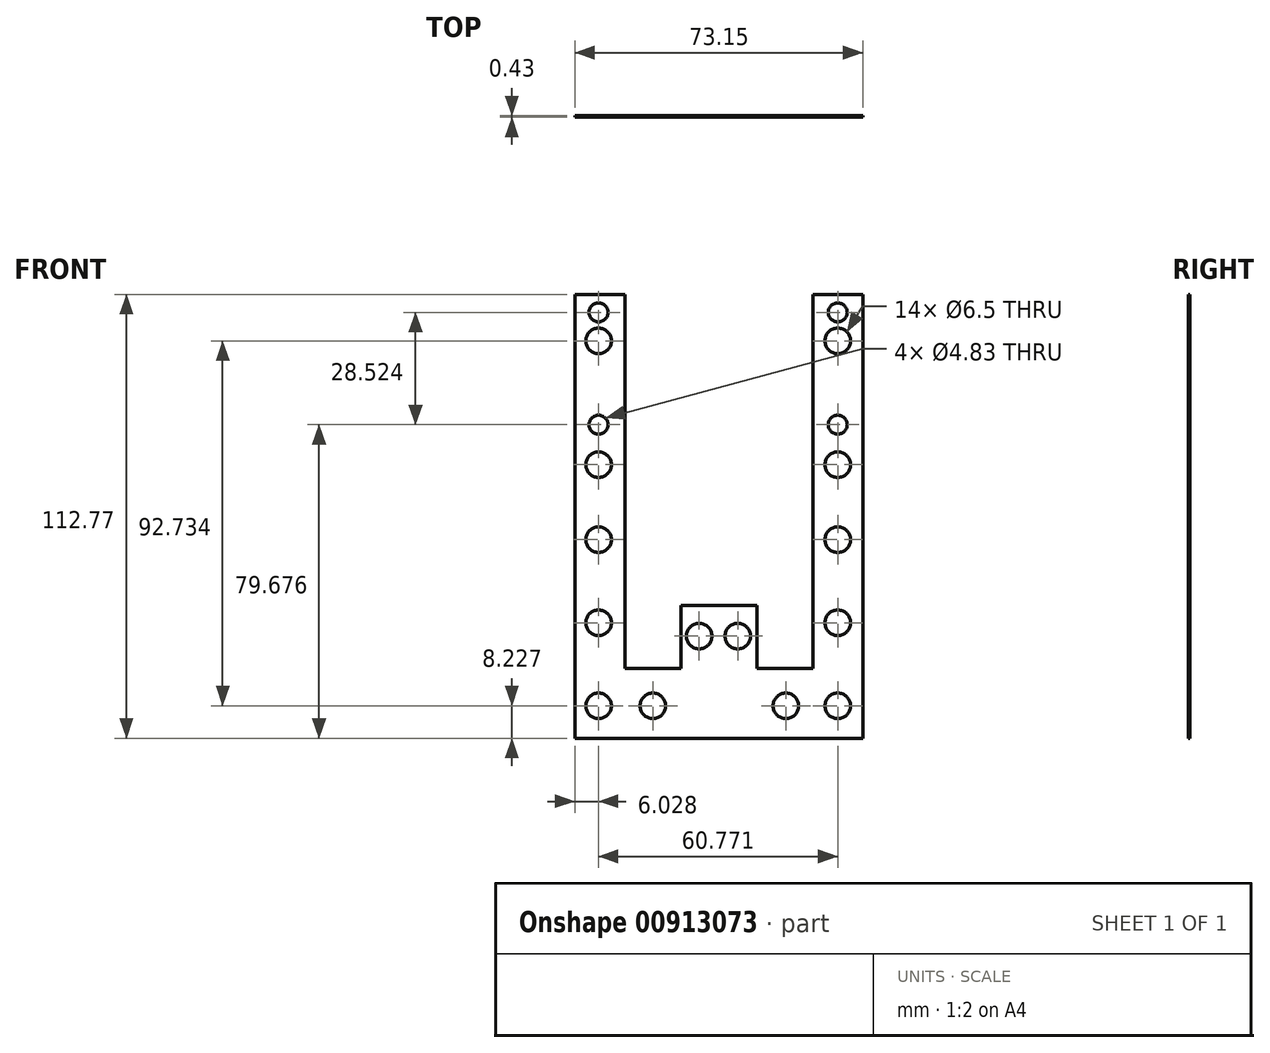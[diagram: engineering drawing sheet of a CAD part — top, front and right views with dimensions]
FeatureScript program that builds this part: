
annotation { "Feature Type Name" : "Feature", "Feature Type Description" : "" }
export const myFeature = defineFeature(function(context is Context, id is Id, definition is map)
    precondition{}
    {
        {
            var Q0;
            Q0=qCreatedBy(makeId("Front.planeOp"),FACE);
            var sketch = newSketch(context, id + "F0", { "sketchPlane" : qUnion([Q0])});
            skLineSegment(sketch, "E0", {"start": v(-36.05, 56.48) * mm, "end": v(-36.05, -56.3) * mm});
            skLineSegment(sketch, "E1", {"start": v(-36.05, -56.3) * mm, "end": v(37.1, -56.3) * mm});
            skLineSegment(sketch, "E2", {"start": v(37.1, -56.3) * mm, "end": v(37.1, 56.48) * mm});
            skLineSegment(sketch, "E3", {"start": v(37.1, 56.48) * mm, "end": v(24.4, 56.48) * mm});
            skLineSegment(sketch, "E4", {"start": v(-36.05, 56.48) * mm, "end": v(-23.35, 56.48) * mm});
            skLineSegment(sketch, "E5", {"start": v(24.4, 56.48) * mm, "end": v(24.4, -38.51) * mm});
            skLineSegment(sketch, "E6", {"start": v(-23.35, 56.48) * mm, "end": v(-23.35, -38.51) * mm});
            skLineSegment(sketch, "E7", {"start": v(-23.35, -38.51) * mm, "end": v(-9.13, -38.51) * mm});
            skLineSegment(sketch, "E8", {"start": v(24.4, -38.51) * mm, "end": v(10.17, -38.51) * mm});
            skLineSegment(sketch, "E9", {"start": v(10.17, -38.51) * mm, "end": v(10.17, -22.51) * mm});
            skLineSegment(sketch, "E10", {"start": v(-9.13, -38.51) * mm, "end": v(-9.13, -22.51) * mm});
            skLineSegment(sketch, "E11", {"start": v(-9.13, -22.51) * mm, "end": v(10.17, -22.51) * mm});
            skCircle(sketch, "E12", {"center": v(30.75, 51.91) * mm, "radius": 2.41 * mm});
            skCircle(sketch, "E13", {"center": v(-30.02, 51.91) * mm, "radius": 2.41 * mm});
            skCircle(sketch, "E14", {"center": v(30.75, 23.39) * mm, "radius": 2.41 * mm});
            skCircle(sketch, "E15", {"center": v(-30.02, 23.39) * mm, "radius": 2.41 * mm});
            skCircle(sketch, "E16", {"center": v(-30.02, 44.67) * mm, "radius": 3.25 * mm});
            skCircle(sketch, "E17", {"center": v(30.75, 44.67) * mm, "radius": 3.25 * mm});
            skCircle(sketch, "E18", {"center": v(-30.02, 13.2) * mm, "radius": 3.25 * mm});
            skCircle(sketch, "E19", {"center": v(30.75, 13.2) * mm, "radius": 3.25 * mm});
            skCircle(sketch, "E20", {"center": v(-30.02, -5.84) * mm, "radius": 3.25 * mm});
            skCircle(sketch, "E21", {"center": v(30.75, -5.84) * mm, "radius": 3.25 * mm});
            skCircle(sketch, "E22", {"center": v(-30.02, -26.95) * mm, "radius": 3.25 * mm});
            skCircle(sketch, "E23", {"center": v(30.75, -26.95) * mm, "radius": 3.25 * mm});
            skCircle(sketch, "E24", {"center": v(-30.02, -48.06) * mm, "radius": 3.25 * mm});
            skCircle(sketch, "E25", {"center": v(30.75, -48.06) * mm, "radius": 3.25 * mm});
            skCircle(sketch, "E26", {"center": v(-16.22, -48.06) * mm, "radius": 3.25 * mm});
            skCircle(sketch, "E27", {"center": v(17.56, -48.06) * mm, "radius": 3.25 * mm});
            skCircle(sketch, "E28", {"center": v(-4.47, -30.33) * mm, "radius": 3.25 * mm});
            skCircle(sketch, "E29", {"center": v(5.35, -30.33) * mm, "radius": 3.25 * mm});
            skSolve(sketch);
        }
        {
            var Q0;
            Q0=qSketchRegion(id+"F0",true);
            extrude(context, id + "F1", {"entities" : qUnion([Q0]), "depth" : 0.43 * mm, "offsetDistance" : 25.4 * mm});
        }
    });
